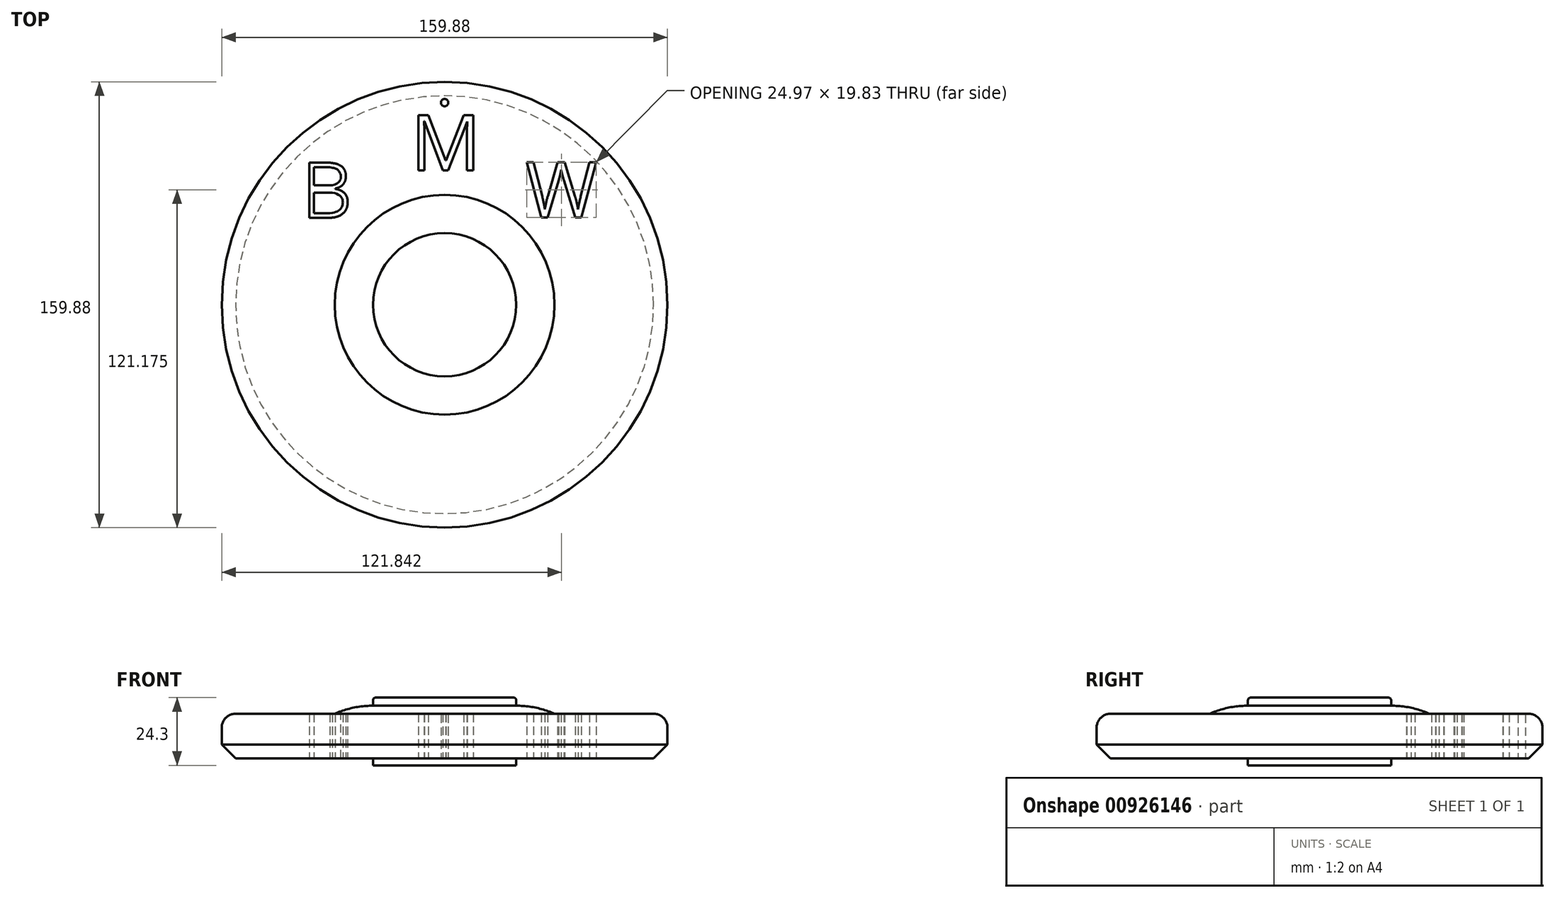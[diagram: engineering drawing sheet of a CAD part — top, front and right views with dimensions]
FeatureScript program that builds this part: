
annotation { "Feature Type Name" : "Feature", "Feature Type Description" : "" }
export const myFeature = defineFeature(function(context is Context, id is Id, definition is map)
    precondition{}
    {
        {
            var Q0;
            Q0=qCreatedBy(makeId("Top.planeOp"),FACE);
            var sketch = newSketch(context, id + "F0", { "sketchPlane" : qUnion([Q0])});
            skText(sketch, "E0", { "text": "M", "fontName": "OpenSans-Regular.ttf"});
            skText(sketch, "E1", { "text": "B", "fontName": "OpenSans-Regular.ttf"});
            skText(sketch, "E2", { "text": "W\n", "fontName": "OpenSans-Regular.ttf"});
            skCircle(sketch, "E3", {"center": v(0, 0) * mm, "radius": 41.51 * mm});
            skCircle(sketch, "E4", {"center": v(0, 0) * mm, "radius": 79.94 * mm});
            skLineSegment(sketch, "E5", {"start": v(0, 0) * mm, "end": v(41.51, 0) * mm});
            skLineSegment(sketch, "E6", {"start": v(0, 0) * mm, "end": v(-41.51, 0) * mm});
            skLineSegment(sketch, "E7", {"start": v(0, -41.51) * mm, "end": v(0, 41.51) * mm});
            const initialGuessF0  = {"E0": [-0.01208, 0.04822, 1, 0, 0.02], "E1": [-0.05122, 0.03118, 1, 0, 0.02], "E2": [0.02905, 0.03132, 1, 0, 0.02]};
            skSetInitialGuess(sketch, initialGuessF0);
            skSolve(sketch);
        }
        {
            var Q0;
            {var subQ0=sQuery(id+"F0.wireOp",EDGE,"E6");Q0=makeQuery(id+"F0.imprint","IMPRINT",FACE,{"disambiguationData":[TD([[makeQuery(id+"F0.imprint","IMPRINT",EDGE,{"derivedFrom":subQ0}),-1.0]])]});}
            var Q1;
            {var subQ0=sQuery(id+"F0.wireOp",EDGE,"E5");Q1=makeQuery(id+"F0.imprint","IMPRINT",FACE,{"disambiguationData":[TD([[makeQuery(id+"F0.imprint","IMPRINT",EDGE,{"derivedFrom":subQ0}),1.0]])]});}
            var Q2;
            {var subQ0=sQuery(id+"F0.wireOp",EDGE,"E6");Q2=makeQuery(id+"F0.imprint","IMPRINT",FACE,{"disambiguationData":[TD([[makeQuery(id+"F0.imprint","IMPRINT",EDGE,{"derivedFrom":subQ0}),1.0]])]});}
            var Q3;
            {var subQ0=sQuery(id+"F0.wireOp",EDGE,"E5");Q3=makeQuery(id+"F0.imprint","IMPRINT",FACE,{"disambiguationData":[TD([[makeQuery(id+"F0.imprint","IMPRINT",EDGE,{"derivedFrom":subQ0}),-1.0]])]});}
            extrude(context, id + "F1", {"entities" : qUnion([Q0, Q1, Q2, Q3]), "depth" : 18.9 * mm, "offsetDistance" : 25 * mm});
        }
        {
            var Q0;
            Q0 = qSketchRegion(id + "F0", true);
            extrude(context, id + "F2", {"entities" : qUnion([Q0]), "operationType" : NewBodyOperationType.ADD, "depth" : 16 * mm, "offsetDistance" : 25 * mm});
        }
        {
            var Q0;
            Q0=makeQuery(id+"F1.opExtrude","CAP_EDGE",EDGE,{"disambiguationData":[OSD([sQuery(id+"F0.wireOp",EDGE,"E3")])],"isStart":false});
            chamfer(context, id + "F3", {"entities" : qUnion([Q0]), "width" : 5 * mm, "tangentPropagation" : true});
        }
        {
            var Q0;
            Q0=makeQuery(id+"F2.opExtrude","CAP_EDGE",EDGE,{"disambiguationData":[OSD([sQuery(id+"F0.wireOp",EDGE,"E4")])],"isStart":false});
            fillet(context, id + "F4", {"entities" : qUnion([Q0]), "radius" : 5 * mm, "tangentPropagation" : true, "allowEdgeOverflow" : false});
        }
        {
            var Q0;
            Q0=makeQuery(id+"F2.opExtrude","CAP_EDGE",EDGE,{"disambiguationData":[OSD([sQuery(id+"F0.wireOp",EDGE,"E4")])],"isStart":true});
            chamfer(context, id + "F5", {"entities" : qUnion([Q0]), "width" : 5 * mm, "tangentPropagation" : true});
        }
        {
            var Q0;
            Q0=makeQuery(id+"F1.opExtrude","CAP_FACE",FACE,{"disambiguationData":[OSD([sQuery(id+"F0.wireOp",EDGE,"E3")])],"isStart":false});
            extrude(context, id + "F6", {"entities" : qUnion([Q0]), "operationType" : NewBodyOperationType.ADD, "oppositeDirection" : true, "depth" : 3 * mm, "offsetDistance" : 25 * mm});
        }
        {
            var Q0;
            {var subQ0=sQuery(id+"F0.wireOp",EDGE,"E3");Q0=makeQuery(id+"F3.opChamfer","BLEND_EDGE",EDGE,{"blendedFrom":[makeQuery(id+"F1.opExtrude","CAP_EDGE",EDGE,{"disambiguationData":[OSD([subQ0])],"isStart":false}),makeQuery(id+"F1.opExtrude","CAP_FACE",FACE,{"disambiguationData":[OSD([subQ0])],"isStart":false})],"blendedInto":[makeQuery(id+"F1.opExtrude","CAP_FACE",FACE,{"disambiguationData":[OSD([subQ0])],"isStart":false})]});}
            var Q1;
            Q1=makeQuery(id+"F1.opExtrude","CAP_FACE",FACE,{"disambiguationData":[OSD([sQuery(id+"F0.wireOp",EDGE,"E3")])],"isStart":false});
            fillet(context, id + "F7", {"entities" : qUnion([Q0, Q1]), "radius" : 33.98 * mm, "tangentPropagation" : true, "allowEdgeOverflow" : false});
        }
        {
            var Q0;
            Q0=makeQuery(id+"F1.opExtrude","CAP_FACE",FACE,{"disambiguationData":[OSD([sQuery(id+"F0.wireOp",EDGE,"E3")])],"isStart":false});
            extrude(context, id + "F8", {"entities" : qUnion([Q0]), "operationType" : NewBodyOperationType.ADD, "depth" : 2.9 * mm, "offsetDistance" : 25 * mm});
        }
        {
            var Q0;
            Q0=qCreatedBy(makeId("Top.planeOp"),FACE);
            var sketch = newSketch(context, id + "F9", { "sketchPlane" : qUnion([Q0])});
            skLineSegment(sketch, "E8", {"start": v(0, 26.15) * mm, "end": v(0, -25.48) * mm});
            skLineSegment(sketch, "E9", {"start": v(-25.9, 0) * mm, "end": v(24.83, 0) * mm});
            skSolve(sketch);
        }
        {
            var Q0;
            Q0=qCreatedBy(makeId("Top.planeOp"),FACE);
            var sketch = newSketch(context, id + "F10", { "sketchPlane" : qUnion([Q0])});
            skLineSegment(sketch, "E10.bottom", {"start": v(-25.64, 0.52) * mm, "end": v(-0.52, 0.52) * mm});
            skLineSegment(sketch, "E11", {"start": v(-25.68, -0.58) * mm, "end": v(-0.52, -0.58) * mm});
            skLineSegment(sketch, "E12", {"start": v(-0.52, 25.67) * mm, "end": v(-0.52, 0.52) * mm});
            skLineSegment(sketch, "E13", {"start": v(0.56, 25.67) * mm, "end": v(0.56, 0.52) * mm});
            skLineSegment(sketch, "E14", {"start": v(-0.52, -0.58) * mm, "end": v(-0.52, -25.45) * mm});
            skLineSegment(sketch, "E15", {"start": v(0.56, -0.58) * mm, "end": v(0.56, -25.54) * mm});
            skLineSegment(sketch, "E16.trimOffspring", {"start": v(0.56, 0.52) * mm, "end": v(25.62, 0.52) * mm});
            skLineSegment(sketch, "E17.trimOffspring", {"start": v(0.56, -0.58) * mm, "end": v(25.58, -0.58) * mm});
            skPoint(sketch, "E18.start.orphan", {"position": v(0, 124.4) * mm});
            skSolve(sketch);
        }
        {
            var Q0;
            Q0=qCreatedBy(makeId("Top.planeOp"),FACE);
            var sketch = newSketch(context, id + "F11", { "sketchPlane" : qUnion([Q0])});
            skLineSegment(sketch, "E19", {"start": v(-46.92, 49.32) * mm, "end": v(-46.92, 42.82) * mm});
            skLineSegment(sketch, "E20", {"start": v(-46.92, 49.32) * mm, "end": v(-41.12, 49.32) * mm});
            skLineSegment(sketch, "E21", {"start": v(-46.92, 32.81) * mm, "end": v(-41.12, 32.81) * mm});
            skFitSpline(sketch, "E22", {"points": [v(-41.12, 49.32) * mm, v(-37.9, 47.94) * mm, v(-40.2, 42.82) * mm], "startDerivative": vector(13, -2.78) * mm, "endDerivative": vector(-21.77, -6.74) * mm});
            skFitSpline(sketch, "E23", {"points": [v(-41.12, 32.81) * mm, v(-36.54, 36.17) * mm, v(-40.2, 40.22) * mm], "startDerivative": vector(19.74, 2.15) * mm, "endDerivative": vector(-20.45, 4.1) * mm});
            skLineSegment(sketch, "E24", {"start": v(-40.2, 42.82) * mm, "end": v(-44.35, 42.82) * mm});
            skLineSegment(sketch, "E25", {"start": v(-40.2, 40.22) * mm, "end": v(-44.35, 40.22) * mm});
            skLineSegment(sketch, "E26", {"start": v(-44.35, 42.82) * mm, "end": v(-46.92, 42.82) * mm});
            skLineSegment(sketch, "E27", {"start": v(-44.35, 40.22) * mm, "end": v(-46.92, 40.22) * mm});
            skLineSegment(sketch, "E28.trimOffspring", {"start": v(-46.92, 40.22) * mm, "end": v(-46.92, 32.81) * mm});
            skSolve(sketch);
        }
        {
            var Q0;
            Q0 = qSketchRegion(id + "F11", true);
            extrude(context, id + "F12", {"entities" : qUnion([Q0]), "depth" : 16 * mm, "offsetDistance" : 25 * mm});
        }
        {
            var Q0;
            Q0 = qSketchRegion(id + "F10", true);
            var Q1;
            Q1=makeQuery(id+"F8.opExtrude","CAP_FACE",FACE,{"disambiguationData":[OSD([sQuery(id+"F0.wireOp",EDGE,"E3")])],"isStart":false});
            extrude(context, id + "F13", {"entities" : qUnion([Q0, Q1]), "operationType" : NewBodyOperationType.ADD, "oppositeDirection" : true, "depth" : 24.3 * mm, "offsetDistance" : 25 * mm});
        }
        {
            var Q0;
            Q0=sQuery(id+"F10.wireOp",EDGE,"E14");
            var Q1;
            Q1=sQuery(id+"F10.wireOp",EDGE,"E13");
            var Q2;
            Q2=sQuery(id+"F9.wireOp",EDGE,"E9");
            var Q3;
            Q3=sQuery(id+"F10.wireOp",EDGE,"E12");
            var Q4;
            Q4=sQuery(id+"F10.wireOp",EDGE,"E15");
            var Q5;
            Q5=sQuery(id+"F10.wireOp",EDGE,"E11");
            var Q6;
            Q6=sQuery(id+"F10.wireOp",EDGE,"E10.bottom");
            var Q7;
            Q7=sQuery(id+"F10.wireOp",EDGE,"E16.trimOffspring");
            var Q8;
            Q8=sQuery(id+"F10.wireOp",EDGE,"E17.trimOffspring");
            extrude(context, id + "F14", {"bodyType" : ToolBodyType.SURFACE, "surfaceEntities" : qUnion([Q0, Q1, Q2, Q3, Q4, Q5, Q6, Q7, Q8]), "depth" : 25 * mm, "offsetDistance" : 25 * mm});
        }
        {
            var Q0;
            Q0=makeQuery(id+"F8.opExtrude","CAP_EDGE",EDGE,{"disambiguationData":[OSD([sQuery(id+"F0.wireOp",EDGE,"E3")])],"isStart":false});
            fillet(context, id + "F15", {"entities" : qUnion([Q0]), "radius" : 0.97 * mm, "tangentPropagation" : true, "allowEdgeOverflow" : false});
        }
        {
            var Q0;
            Q0=qCreatedBy(makeId("Top.planeOp"),FACE);
            var sketch = newSketch(context, id + "F16", { "sketchPlane" : qUnion([Q0])});
            skCircle(sketch, "E29", {"center": v(0, 71.36) * mm, "radius": 2.28 * mm});
            skSolve(sketch);
        }
        {
            var Q0;
            Q0 = qSketchRegion(id + "F16", true);
            extrude(context, id + "F17", {"entities" : qUnion([Q0]), "operationType" : NewBodyOperationType.REMOVE, "oppositeDirection" : true, "depth" : 48.9 * mm, "offsetDistance" : 25 * mm});
        }
        {
            var Q0;
            Q0=qCreatedBy(makeId("Top.planeOp"),FACE);
            var sketch = newSketch(context, id + "F18", { "sketchPlane" : qUnion([Q0])});
            skCircle(sketch, "E30", {"center": v(0, 72.52) * mm, "radius": 1.31 * mm});
            skCircle(sketch, "E31", {"center": v(0, 72.52) * mm, "radius": 0.64 * mm});
            skSolve(sketch);
        }
        {
            var Q0;
            Q0 = qSketchRegion(id + "F18", true);
            extrude(context, id + "F19", {"entities" : qUnion([Q0]), "operationType" : NewBodyOperationType.REMOVE, "depth" : 41.5 * mm, "offsetDistance" : 25 * mm});
        }
        {
            var Q0;
            Q0 = qSketchRegion(id + "F18", true);
            var Q1;
            Q1=makeQuery(id+"F19.boolean.opBoolean","SPLIT",FACE,{"disambiguationData":[TD([makeQuery(id+"F19.opExtrude","SWEPT_FACE",FACE,{"disambiguationData":[OSD([sQuery(id+"F18.wireOp",EDGE,"E31")])]})])],"derivedFrom":makeQuery(id+"F2.opExtrude","CAP_FACE",FACE,{"disambiguationData":[OSD([sQuery(id+"F0.wireOp",EDGE,"E0.sketch_text.stroke-0"),sQuery(id+"F0.wireOp",EDGE,"E0.sketch_text.stroke-1"),sQuery(id+"F0.wireOp",EDGE,"E0.sketch_text.stroke-2"),sQuery(id+"F0.wireOp",EDGE,"E0.sketch_text.stroke-3"),sQuery(id+"F0.wireOp",EDGE,"E0.sketch_text.stroke-4"),sQuery(id+"F0.wireOp",EDGE,"E0.sketch_text.stroke-5"),sQuery(id+"F0.wireOp",EDGE,"E0.sketch_text.stroke-6"),sQuery(id+"F0.wireOp",EDGE,"E0.sketch_text.stroke-7"),sQuery(id+"F0.wireOp",EDGE,"E0.sketch_text.stroke-8"),sQuery(id+"F0.wireOp",EDGE,"E0.sketch_text.stroke-9"),sQuery(id+"F0.wireOp",EDGE,"E0.sketch_text.stroke-10"),sQuery(id+"F0.wireOp",EDGE,"E0.sketch_text.stroke-11"),sQuery(id+"F0.wireOp",EDGE,"E0.sketch_text.stroke-12"),sQuery(id+"F0.wireOp",EDGE,"E0.sketch_text.stroke-13"),sQuery(id+"F0.wireOp",EDGE,"E0.sketch_text.stroke-14"),sQuery(id+"F0.wireOp",EDGE,"E0.sketch_text.stroke-15"),sQuery(id+"F0.wireOp",EDGE,"E0.sketch_text.stroke-16"),sQuery(id+"F0.wireOp",EDGE,"E0.sketch_text.stroke-17"),sQuery(id+"F0.wireOp",EDGE,"E1.sketch_text.stroke-0"),sQuery(id+"F0.wireOp",EDGE,"E1.sketch_text.stroke-1"),sQuery(id+"F0.wireOp",EDGE,"E1.sketch_text.stroke-2"),sQuery(id+"F0.wireOp",EDGE,"E1.sketch_text.stroke-3"),sQuery(id+"F0.wireOp",EDGE,"E1.sketch_text.stroke-4"),sQuery(id+"F0.wireOp",EDGE,"E1.sketch_text.stroke-5"),sQuery(id+"F0.wireOp",EDGE,"E1.sketch_text.stroke-6"),sQuery(id+"F0.wireOp",EDGE,"E1.sketch_text.stroke-7"),sQuery(id+"F0.wireOp",EDGE,"E1.sketch_text.stroke-8"),sQuery(id+"F0.wireOp",EDGE,"E1.sketch_text.stroke-9"),sQuery(id+"F0.wireOp",EDGE,"E1.sketch_text.stroke-10"),sQuery(id+"F0.wireOp",EDGE,"E2.sketch_text.stroke-0"),sQuery(id+"F0.wireOp",EDGE,"E2.sketch_text.stroke-1"),sQuery(id+"F0.wireOp",EDGE,"E2.sketch_text.stroke-2"),sQuery(id+"F0.wireOp",EDGE,"E2.sketch_text.stroke-3"),sQuery(id+"F0.wireOp",EDGE,"E2.sketch_text.stroke-4"),sQuery(id+"F0.wireOp",EDGE,"E2.sketch_text.stroke-5"),sQuery(id+"F0.wireOp",EDGE,"E2.sketch_text.stroke-6"),sQuery(id+"F0.wireOp",EDGE,"E2.sketch_text.stroke-7"),sQuery(id+"F0.wireOp",EDGE,"E2.sketch_text.stroke-8"),sQuery(id+"F0.wireOp",EDGE,"E2.sketch_text.stroke-9"),sQuery(id+"F0.wireOp",EDGE,"E2.sketch_text.stroke-10"),sQuery(id+"F0.wireOp",EDGE,"E2.sketch_text.stroke-11"),sQuery(id+"F0.wireOp",EDGE,"E2.sketch_text.stroke-12"),sQuery(id+"F0.wireOp",EDGE,"E2.sketch_text.stroke-13"),sQuery(id+"F0.wireOp",EDGE,"E2.sketch_text.stroke-14"),sQuery(id+"F0.wireOp",EDGE,"E2.sketch_text.stroke-15"),sQuery(id+"F0.wireOp",EDGE,"E2.sketch_text.stroke-16"),sQuery(id+"F0.wireOp",EDGE,"E2.sketch_text.stroke-17"),sQuery(id+"F0.wireOp",EDGE,"E2.sketch_text.stroke-18"),sQuery(id+"F0.wireOp",EDGE,"E2.sketch_text.stroke-19"),sQuery(id+"F0.wireOp",EDGE,"E3"),sQuery(id+"F0.wireOp",EDGE,"E4")])],"isStart":false})});
            extrude(context, id + "F20", {"entities" : qUnion([Q0, Q1]), "operationType" : NewBodyOperationType.REMOVE, "oppositeDirection" : true, "depth" : 21.5 * mm, "offsetDistance" : 25 * mm});
        }
        {
            var Q0;
            Q0=makeQuery(id+"F19.boolean.opBoolean","INTERSECT",EDGE,{"derivedFrom":[makeQuery(id+"F2.opExtrude","CAP_FACE",FACE,{"disambiguationData":[OSD([sQuery(id+"F0.wireOp",EDGE,"E0.sketch_text.stroke-0"),sQuery(id+"F0.wireOp",EDGE,"E0.sketch_text.stroke-1"),sQuery(id+"F0.wireOp",EDGE,"E0.sketch_text.stroke-2"),sQuery(id+"F0.wireOp",EDGE,"E0.sketch_text.stroke-3"),sQuery(id+"F0.wireOp",EDGE,"E0.sketch_text.stroke-4"),sQuery(id+"F0.wireOp",EDGE,"E0.sketch_text.stroke-5"),sQuery(id+"F0.wireOp",EDGE,"E0.sketch_text.stroke-6"),sQuery(id+"F0.wireOp",EDGE,"E0.sketch_text.stroke-7"),sQuery(id+"F0.wireOp",EDGE,"E0.sketch_text.stroke-8"),sQuery(id+"F0.wireOp",EDGE,"E0.sketch_text.stroke-9"),sQuery(id+"F0.wireOp",EDGE,"E0.sketch_text.stroke-10"),sQuery(id+"F0.wireOp",EDGE,"E0.sketch_text.stroke-11"),sQuery(id+"F0.wireOp",EDGE,"E0.sketch_text.stroke-12"),sQuery(id+"F0.wireOp",EDGE,"E0.sketch_text.stroke-13"),sQuery(id+"F0.wireOp",EDGE,"E0.sketch_text.stroke-14"),sQuery(id+"F0.wireOp",EDGE,"E0.sketch_text.stroke-15"),sQuery(id+"F0.wireOp",EDGE,"E0.sketch_text.stroke-16"),sQuery(id+"F0.wireOp",EDGE,"E0.sketch_text.stroke-17"),sQuery(id+"F0.wireOp",EDGE,"E1.sketch_text.stroke-0"),sQuery(id+"F0.wireOp",EDGE,"E1.sketch_text.stroke-1"),sQuery(id+"F0.wireOp",EDGE,"E1.sketch_text.stroke-2"),sQuery(id+"F0.wireOp",EDGE,"E1.sketch_text.stroke-3"),sQuery(id+"F0.wireOp",EDGE,"E1.sketch_text.stroke-4"),sQuery(id+"F0.wireOp",EDGE,"E1.sketch_text.stroke-5"),sQuery(id+"F0.wireOp",EDGE,"E1.sketch_text.stroke-6"),sQuery(id+"F0.wireOp",EDGE,"E1.sketch_text.stroke-7"),sQuery(id+"F0.wireOp",EDGE,"E1.sketch_text.stroke-8"),sQuery(id+"F0.wireOp",EDGE,"E1.sketch_text.stroke-9"),sQuery(id+"F0.wireOp",EDGE,"E1.sketch_text.stroke-10"),sQuery(id+"F0.wireOp",EDGE,"E2.sketch_text.stroke-0"),sQuery(id+"F0.wireOp",EDGE,"E2.sketch_text.stroke-1"),sQuery(id+"F0.wireOp",EDGE,"E2.sketch_text.stroke-2"),sQuery(id+"F0.wireOp",EDGE,"E2.sketch_text.stroke-3"),sQuery(id+"F0.wireOp",EDGE,"E2.sketch_text.stroke-4"),sQuery(id+"F0.wireOp",EDGE,"E2.sketch_text.stroke-5"),sQuery(id+"F0.wireOp",EDGE,"E2.sketch_text.stroke-6"),sQuery(id+"F0.wireOp",EDGE,"E2.sketch_text.stroke-7"),sQuery(id+"F0.wireOp",EDGE,"E2.sketch_text.stroke-8"),sQuery(id+"F0.wireOp",EDGE,"E2.sketch_text.stroke-9"),sQuery(id+"F0.wireOp",EDGE,"E2.sketch_text.stroke-10"),sQuery(id+"F0.wireOp",EDGE,"E2.sketch_text.stroke-11"),sQuery(id+"F0.wireOp",EDGE,"E2.sketch_text.stroke-12"),sQuery(id+"F0.wireOp",EDGE,"E2.sketch_text.stroke-13"),sQuery(id+"F0.wireOp",EDGE,"E2.sketch_text.stroke-14"),sQuery(id+"F0.wireOp",EDGE,"E2.sketch_text.stroke-15"),sQuery(id+"F0.wireOp",EDGE,"E2.sketch_text.stroke-16"),sQuery(id+"F0.wireOp",EDGE,"E2.sketch_text.stroke-17"),sQuery(id+"F0.wireOp",EDGE,"E2.sketch_text.stroke-18"),sQuery(id+"F0.wireOp",EDGE,"E2.sketch_text.stroke-19"),sQuery(id+"F0.wireOp",EDGE,"E3"),sQuery(id+"F0.wireOp",EDGE,"E4")])],"isStart":false}),makeQuery(id+"F19.opExtrude","SWEPT_FACE",FACE,{"disambiguationData":[OSD([sQuery(id+"F18.wireOp",EDGE,"E30")])]})]});
            fillet(context, id + "F21", {"entities" : qUnion([Q0]), "radius" : 0.34 * mm, "tangentPropagation" : true, "allowEdgeOverflow" : false});
        }
    });
